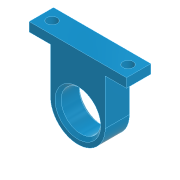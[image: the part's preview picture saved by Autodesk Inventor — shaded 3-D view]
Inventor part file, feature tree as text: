
AUTODESK INVENTOR PART (.ipt)
format: ipt  version: 2022 (Build 260153000, 153)  size: 150,016 bytes
history: native  units: mm
features: projected_geometry x3, extrude x2, sketch x2, hole x1, chamfer x1
ambient origin geometry x8: Origin, YZ Plane, XZ Plane, XY Plane, X Axis, Y Axis, Z Axis, Center Point
bodies: Solid1 (feature_tree)
feature tree (9):
  extrude  "Extrusion1"  Depth=10.0mm
  extrude  "Extrusion2"  Depth=18.0mm
  hole  "Hole1"  [1 undecoded]
  chamfer  "Chamfer2"  Distance=7.0mm
  sketch  "Sketch3"  dims[d2=2.5mm d3=10.0mm]
  sketch  "Sketch4"  dims[d4=1.5mm d5=18.0mm d6=8.0mm d7=0.0mm d8=7.0mm d9=4.0mm d10=0.0mm d11=3.4mm d12=6.0mm d13=6.0mm d14=2.0mm d15=90.0deg d16=8.0mm d17=20.594885mm d22=1.0mm d23=2.0mm d24=45.0deg]
  projected_geometry  "Projected Loop1"
  projected_geometry  "Projected Loop2"
  projected_geometry  "Project Cut Edges1"
note: 1 required parameter value undecoded (feature->parameter linkage not recoverable at this tier; creation-order binding heuristic only, values carry confidence <= 0.55)
